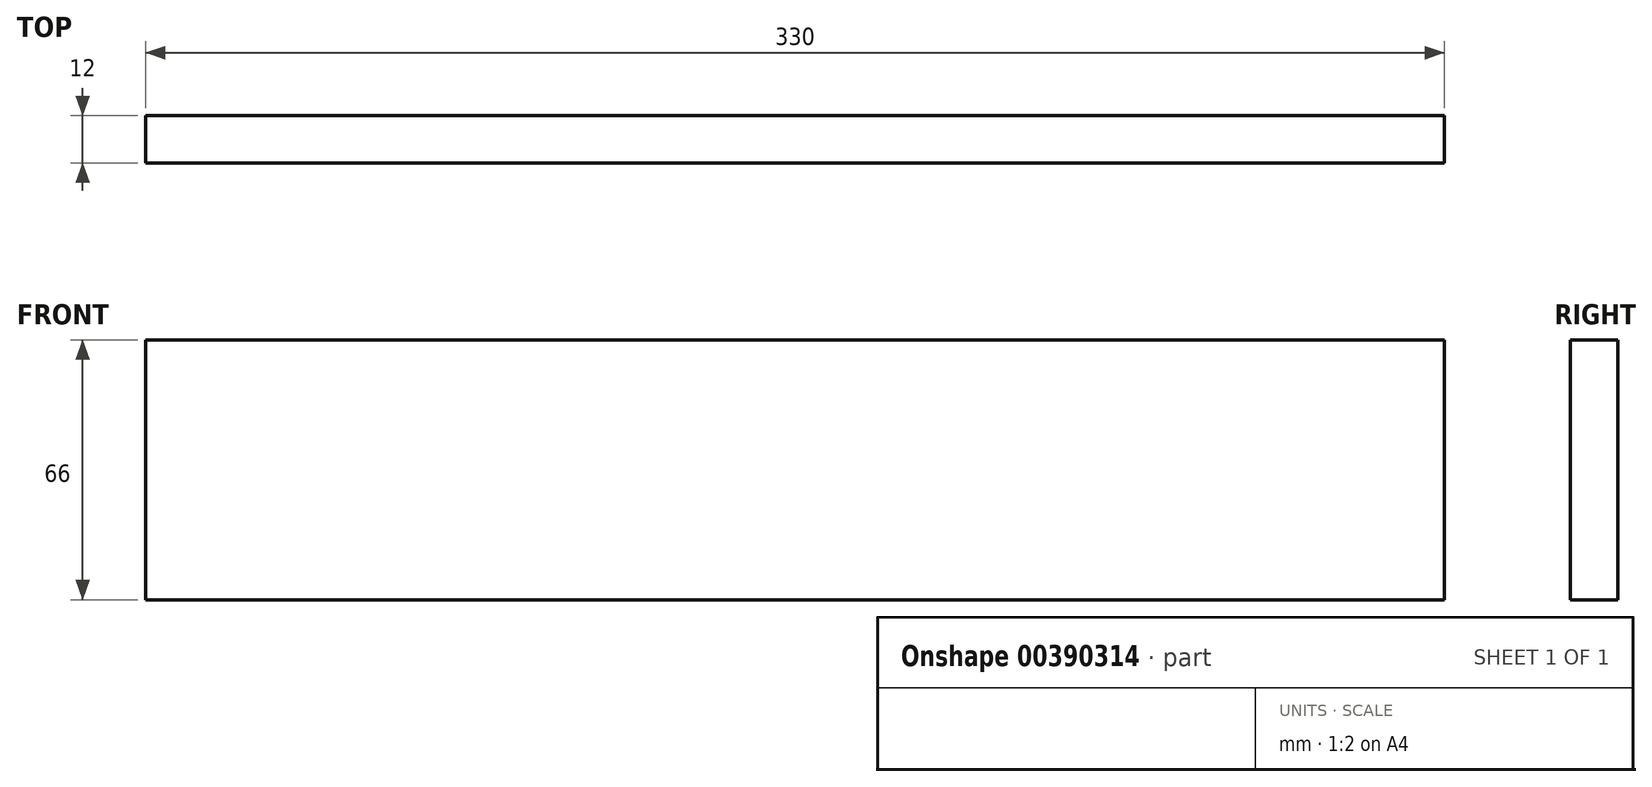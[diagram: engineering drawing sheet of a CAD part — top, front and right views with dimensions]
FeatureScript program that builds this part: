
annotation { "Feature Type Name" : "Feature", "Feature Type Description" : "" }
export const myFeature = defineFeature(function(context is Context, id is Id, definition is map)
    precondition{}
    {
        {
            var Q0;
            Q0=qCreatedBy(makeId("Front.planeOp"),FACE);
            var sketch = newSketch(context, id + "F0", { "sketchPlane" : qUnion([Q0])});
            skLineSegment(sketch, "E0.bottom", {"start": v(0, 0) * mm, "end": v(330, 0) * mm});
            skLineSegment(sketch, "E0.top", {"start": v(0, 66) * mm, "end": v(330, 66) * mm});
            skLineSegment(sketch, "E0.left", {"start": v(0, 0) * mm, "end": v(0, 66) * mm});
            skLineSegment(sketch, "E0.right", {"start": v(330, 0) * mm, "end": v(330, 66) * mm});
            skSolve(sketch);
        }
        {
            var Q0;
            Q0=makeQuery(id+"F0.imprint","IMPRINT",FACE,{"disambiguationData":[TD([[makeQuery(id+"F0.imprint","IMPRINT",EDGE,{"derivedFrom":sQuery(id+"F0.wireOp",EDGE,"E0.bottom")}),1.0]])]});
            extrude(context, id + "F1", {"entities" : qUnion([Q0]), "depth" : 12 * mm});
        }
    });
